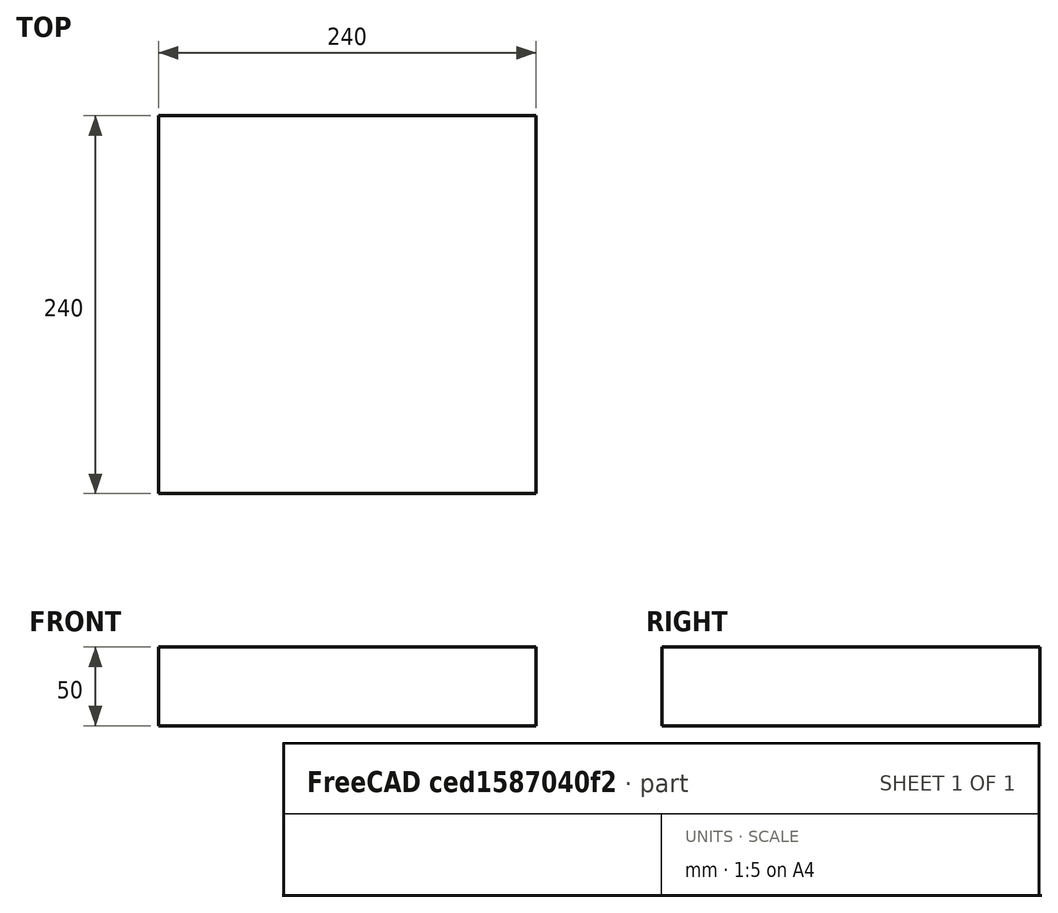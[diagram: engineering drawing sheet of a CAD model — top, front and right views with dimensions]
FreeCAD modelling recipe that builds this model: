
FCSTD DOCUMENT  (FreeCAD 0.15R4671 (Git))
Label: Square Bar 240 EN10059 S235JR
License: All rights reserved
LicenseURL: http://en.wikipedia.org/wiki/All_rights_reserved
objects: Sketcher::SketchObject×1, Part::Extrusion×1
note: 2 computed .brp shape members not serialized (recipe doc carries the construction recipe); baked Part::Feature solids carry a one-line shape summary decoded from their .brp

FEATURE [Sketcher::SketchObject] Sketch
  sketch-geometry (4):
    g0: LineSegment StartX=-120 StartY=-120 StartZ=0 EndX=120 EndY=-120 EndZ=0
    g1: LineSegment StartX=120 StartY=-120 StartZ=0 EndX=120 EndY=120 EndZ=0
    g2: LineSegment StartX=120 StartY=120 StartZ=0 EndX=-120 EndY=120 EndZ=0
    g3: LineSegment StartX=-120 StartY=120 StartZ=0 EndX=-120 EndY=-120 EndZ=0
  constraints (12):
    c: Coincident(g0,g1)
    c: Coincident(g1,g2)
    c: Coincident(g2,g3)
    c: Coincident(g3,g0)
    c: Horizontal(g0)
    c: Horizontal(g2)
    c: Vertical(g1)
    c: Vertical(g3)
    c: Symmetric(g1,g0,g-1)
    c: Symmetric(g2,g1,g-2)
    c: Equal(g1,g2)
    c: DistanceY(g1) = 240
FEATURE [Part::Extrusion] Extrude  label="Square Bar 240 EN10059 S235JR"
  Base = -> Sketch
  Dir = (0,0,50)
  Solid = true
